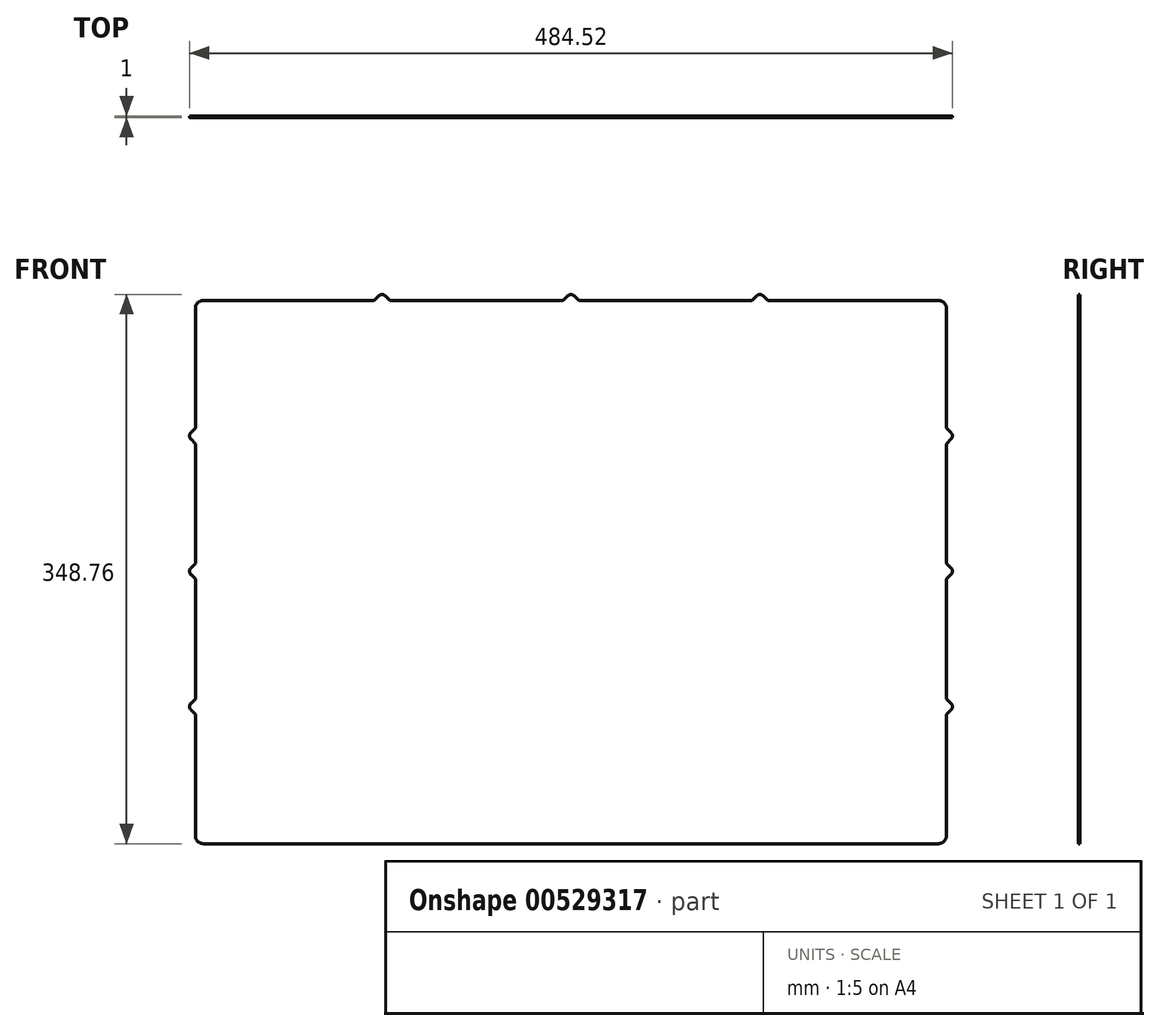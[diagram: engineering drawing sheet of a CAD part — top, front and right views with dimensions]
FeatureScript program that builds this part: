
annotation { "Feature Type Name" : "Feature", "Feature Type Description" : "" }
export const myFeature = defineFeature(function(context is Context, id is Id, definition is map)
    precondition{}
    {
        {
            var Q0;
            Q0=qCreatedBy(makeId("Front.planeOp"),FACE);
            var sketch = newSketch(context, id + "F0", { "sketchPlane" : qUnion([Q0])});
            skLineSegment(sketch, "E0.top", {"start": v(-233.5, 345) * mm, "end": v(-125, 345) * mm});
            skLineSegment(sketch, "E0.left", {"start": v(-238.5, 5) * mm, "end": v(-238.5, 82) * mm});
            skLineSegment(sketch, "E0.right", {"start": v(238.5, 5) * mm, "end": v(238.5, 82) * mm});
            skLineSegment(sketch, "E1", {"start": v(-243.5, 259) * mm, "end": v(243.5, 259) * mm, "construction": true});
            skLineSegment(sketch, "E2", {"start": v(-241.38, 256.88) * mm, "end": v(-238.5, 254) * mm});
            skLineSegment(sketch, "E3", {"start": v(-241.38, 261.12) * mm, "end": v(-238.5, 264) * mm});
            skLineSegment(sketch, "E4", {"start": v(-238.5, 254) * mm, "end": v(238.5, 254) * mm, "construction": true});
            skLineSegment(sketch, "E5", {"start": v(238.5, 254) * mm, "end": v(241.38, 256.88) * mm});
            skLineSegment(sketch, "E6", {"start": v(-238.5, 264) * mm, "end": v(238.5, 264) * mm, "construction": true});
            skLineSegment(sketch, "E7", {"start": v(238.5, 264) * mm, "end": v(241.38, 261.12) * mm});
            skLineSegment(sketch, "E8.trimOffspring", {"start": v(238.5, 264) * mm, "end": v(238.5, 345) * mm});
            skLineSegment(sketch, "E9.trimOffspring", {"start": v(-238.5, 264) * mm, "end": v(-238.5, 340) * mm});
            skLineSegment(sketch, "E10.MirrorCS", {"start": v(238.5, 82) * mm, "end": v(241.38, 84.88) * mm});
            skLineSegment(sketch, "E11.MirrorCS", {"start": v(-238.5, 345) * mm, "end": v(-238.5, 264) * mm});
            skLineSegment(sketch, "E12.MirrorCS", {"start": v(238.5, 340) * mm, "end": v(238.5, 264) * mm});
            skLineSegment(sketch, "E13.MirrorCS", {"start": v(-241.38, 89.12) * mm, "end": v(-238.5, 92) * mm});
            skLineSegment(sketch, "E14.MirrorCS", {"start": v(-241.38, 84.88) * mm, "end": v(-238.5, 82) * mm});
            skLineSegment(sketch, "E15.MirrorCS", {"start": v(238.5, 92) * mm, "end": v(241.38, 89.12) * mm});
            skLineSegment(sketch, "E16.MirrorCS", {"start": v(-238.5, 82) * mm, "end": v(238.5, 82) * mm, "construction": true});
            skLineSegment(sketch, "E17.MirrorCS", {"start": v(-243.5, 87) * mm, "end": v(243.5, 87) * mm, "construction": true});
            skLineSegment(sketch, "E18.MirrorCS", {"start": v(-238.5, 92) * mm, "end": v(238.5, 92) * mm, "construction": true});
            skLineSegment(sketch, "E19.trimOffspring", {"start": v(-238.5, 92) * mm, "end": v(-238.5, 168) * mm});
            skLineSegment(sketch, "E20.trimOffspring", {"start": v(238.5, 92) * mm, "end": v(238.5, 168) * mm});
            skLineSegment(sketch, "E21", {"start": v(-238.5, 178) * mm, "end": v(-241.38, 175.12) * mm});
            skLineSegment(sketch, "E22", {"start": v(-241.38, 170.88) * mm, "end": v(-238.5, 168) * mm});
            skLineSegment(sketch, "E23.MirrorCS", {"start": v(238.5, 178) * mm, "end": v(241.38, 175.12) * mm});
            skLineSegment(sketch, "E24.MirrorCS", {"start": v(241.38, 170.88) * mm, "end": v(238.5, 168) * mm});
            skLineSegment(sketch, "E25", {"start": v(-238.5, 178) * mm, "end": v(238.5, 178) * mm, "construction": true});
            skLineSegment(sketch, "E26", {"start": v(-238.5, 168) * mm, "end": v(238.5, 168) * mm, "construction": true});
            skLineSegment(sketch, "E27.trimOffspring", {"start": v(-238.5, 178) * mm, "end": v(-238.5, 254) * mm});
            skLineSegment(sketch, "E28.trimOffspring", {"start": v(-238.5, 168) * mm, "end": v(-238.5, 92) * mm});
            skLineSegment(sketch, "E29.trimOffspring", {"start": v(238.5, 168) * mm, "end": v(238.5, 92) * mm});
            skLineSegment(sketch, "E30.trimOffspring", {"start": v(238.5, 178) * mm, "end": v(238.5, 254) * mm});
            skLineSegment(sketch, "E31.trimOffspring", {"start": v(238.5, 254) * mm, "end": v(238.5, 178) * mm});
            skLineSegment(sketch, "E32.trimOffspring", {"start": v(-238.5, 254) * mm, "end": v(-238.5, 178) * mm});
            skLineSegment(sketch, "E33", {"start": v(0, -5) * mm, "end": v(0, 350) * mm, "construction": true});
            skPoint(sketch, "E33.endSnap0", {"position": v(0, 345) * mm});
            skLineSegment(sketch, "E34", {"start": v(-120, 350) * mm, "end": v(-120, -4) * mm, "construction": true});
            skLineSegment(sketch, "E35", {"start": v(-125, 345) * mm, "end": v(-122.12, 347.88) * mm});
            skLineSegment(sketch, "E36", {"start": v(-117.88, 347.88) * mm, "end": v(-115, 345) * mm});
            skLineSegment(sketch, "E37", {"start": v(-5, 345) * mm, "end": v(-2.12, 347.88) * mm});
            skLineSegment(sketch, "E38", {"start": v(2.12, 347.88) * mm, "end": v(5, 345) * mm});
            skLineSegment(sketch, "E39", {"start": v(-125, 345) * mm, "end": v(-125, 1) * mm, "construction": true});
            skLineSegment(sketch, "E40", {"start": v(-115, 345) * mm, "end": v(-115, 1) * mm, "construction": true});
            skLineSegment(sketch, "E41", {"start": v(-5, 345) * mm, "end": v(-5, 1) * mm, "construction": true});
            skLineSegment(sketch, "E42", {"start": v(5, 345) * mm, "end": v(5, 1) * mm, "construction": true});
            skLineSegment(sketch, "E43.trimOffspring", {"start": v(-115, 345) * mm, "end": v(-5, 345) * mm});
            skLineSegment(sketch, "E44.trimOffspring", {"start": v(5, 345) * mm, "end": v(115, 345) * mm});
            skLineSegment(sketch, "E45.MirrorCS", {"start": v(117.88, 347.88) * mm, "end": v(115, 345) * mm});
            skLineSegment(sketch, "E46.MirrorCS", {"start": v(125, 345) * mm, "end": v(122.12, 347.88) * mm});
            skLineSegment(sketch, "E47.MirrorCS", {"start": v(125, 345) * mm, "end": v(125, 1) * mm, "construction": true});
            skLineSegment(sketch, "E48.MirrorCS", {"start": v(120, 350) * mm, "end": v(120, -4) * mm, "construction": true});
            skLineSegment(sketch, "E49.MirrorCS", {"start": v(115, 345) * mm, "end": v(115, 1) * mm, "construction": true});
            skLineSegment(sketch, "E50.trimOffspring", {"start": v(125, 345) * mm, "end": v(233.5, 345) * mm});
            skPoint(sketch, "E51.MirrorCS.end.orphan", {"position": v(-120, -5) * mm});
            skPoint(sketch, "E51.MirrorCS.start.orphan", {"position": v(-125, 0) * mm});
            skPoint(sketch, "E52.MirrorCS.end.orphan", {"position": v(-115, 0) * mm});
            skPoint(sketch, "E53.MirrorCS.end.orphan", {"position": v(0, -5) * mm});
            skPoint(sketch, "E53.MirrorCS.start.orphan", {"position": v(-5, 0) * mm});
            skPoint(sketch, "E54.MirrorCS.end.orphan", {"position": v(5, 0) * mm});
            skPoint(sketch, "E55.MirrorCS.end.orphan", {"position": v(120, -5) * mm});
            skPoint(sketch, "E55.MirrorCS.start.orphan", {"position": v(125, 0) * mm});
            skLineSegment(sketch, "E56", {"start": v(-243.5, 173) * mm, "end": v(243.5, 173) * mm, "construction": true});
            skPoint(sketch, "E57.visualSharp", {"position": v(-238.5, 345) * mm});
            skArc(sketch, "E57.filletArc", {"start": v(-233.5, 345) * mm, "mid": v(-237.04, 343.54) * mm, "end": v(-238.5, 340) * mm});
            skPoint(sketch, "E58.visualSharp", {"position": v(-243.5, 259) * mm});
            skArc(sketch, "E58.filletArc", {"start": v(-241.38, 261.12) * mm, "mid": v(-242.26, 259) * mm, "end": v(-241.38, 256.88) * mm});
            skPoint(sketch, "E59.visualSharp", {"position": v(-243.5, 173) * mm});
            skArc(sketch, "E59.filletArc", {"start": v(-241.38, 175.12) * mm, "mid": v(-242.26, 173) * mm, "end": v(-241.38, 170.88) * mm});
            skPoint(sketch, "E60.visualSharp", {"position": v(-243.5, 87) * mm});
            skArc(sketch, "E60.filletArc", {"start": v(-241.38, 89.12) * mm, "mid": v(-242.26, 87) * mm, "end": v(-241.38, 84.88) * mm});
            skPoint(sketch, "E61.visualSharp", {"position": v(243.5, 87) * mm});
            skArc(sketch, "E61.filletArc", {"start": v(241.38, 84.88) * mm, "mid": v(242.26, 87) * mm, "end": v(241.38, 89.12) * mm});
            skPoint(sketch, "E62.visualSharp", {"position": v(243.5, 173) * mm});
            skArc(sketch, "E62.filletArc", {"start": v(241.38, 170.88) * mm, "mid": v(242.26, 173) * mm, "end": v(241.38, 175.12) * mm});
            skPoint(sketch, "E63.visualSharp", {"position": v(243.5, 259) * mm});
            skArc(sketch, "E63.filletArc", {"start": v(241.38, 256.88) * mm, "mid": v(242.26, 259) * mm, "end": v(241.38, 261.12) * mm});
            skPoint(sketch, "E64.visualSharp", {"position": v(120, 350) * mm});
            skArc(sketch, "E64.filletArc", {"start": v(122.12, 347.88) * mm, "mid": v(120, 348.76) * mm, "end": v(117.88, 347.88) * mm});
            skPoint(sketch, "E65.visualSharp", {"position": v(0, 350) * mm});
            skArc(sketch, "E65.filletArc", {"start": v(2.12, 347.88) * mm, "mid": v(0, 348.76) * mm, "end": v(-2.12, 347.88) * mm});
            skPoint(sketch, "E66.visualSharp", {"position": v(-120, 350) * mm});
            skArc(sketch, "E66.filletArc", {"start": v(-117.88, 347.88) * mm, "mid": v(-120, 348.76) * mm, "end": v(-122.12, 347.88) * mm});
            skPoint(sketch, "E67.visualSharp", {"position": v(238.5, 345) * mm});
            skArc(sketch, "E67.filletArc", {"start": v(238.5, 340) * mm, "mid": v(237.04, 343.54) * mm, "end": v(233.5, 345) * mm});
            skPoint(sketch, "E68.visualSharp", {"position": v(238.5, 1) * mm});
            skArc(sketch, "E68.filletArc", {"start": v(233.5, 0) * mm, "mid": v(237.04, 1.46) * mm, "end": v(238.5, 5) * mm});
            skLineSegment(sketch, "E69", {"start": v(233.5, 0) * mm, "end": v(-233.5, 0) * mm});
            skPoint(sketch, "E70.visualSharp", {"position": v(-238.5, 0) * mm});
            skArc(sketch, "E70.filletArc", {"start": v(-238.5, 5) * mm, "mid": v(-237.04, 1.46) * mm, "end": v(-233.5, 0) * mm});
            skSolve(sketch);
        }
        {
            var Q0;
            Q0=qSketchRegion(id+"F0",true);
            extrude(context, id + "F1", {"entities" : qUnion([Q0]), "endBound" : BoundingType.SYMMETRIC, "depth" : 1 * mm, "offsetDistance" : 25 * mm});
        }
    });
